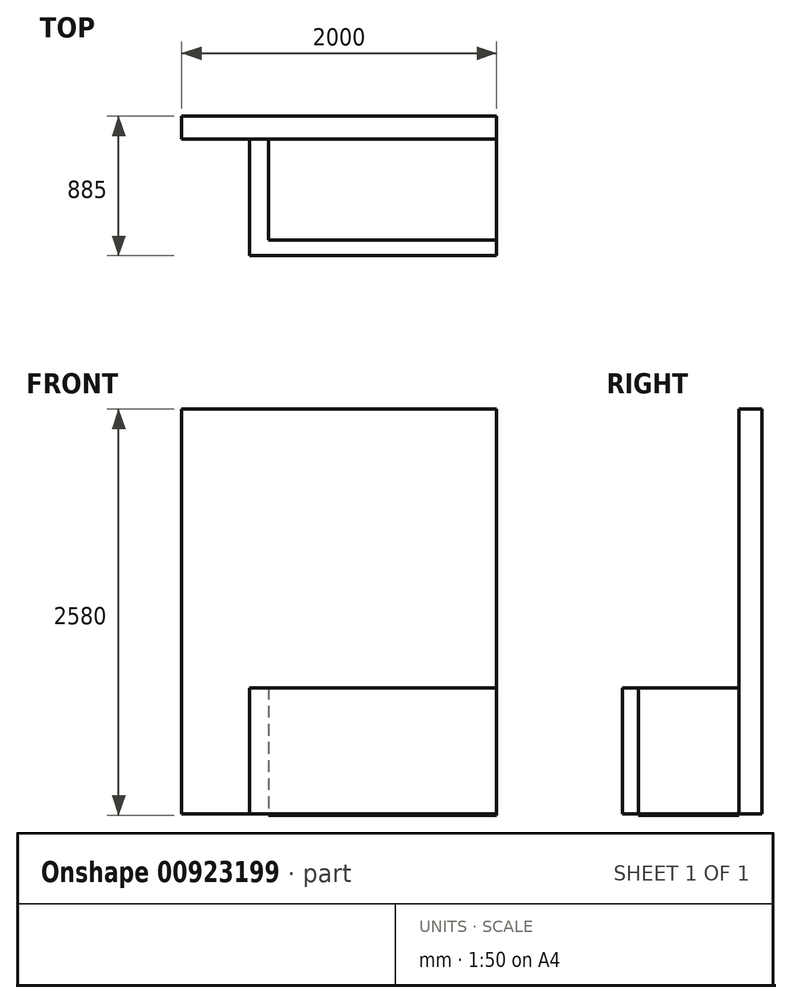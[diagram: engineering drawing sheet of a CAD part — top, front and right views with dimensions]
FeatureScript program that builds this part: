
annotation { "Feature Type Name" : "Feature", "Feature Type Description" : "" }
export const myFeature = defineFeature(function(context is Context, id is Id, definition is map)
    precondition{}
    {
        {
            var Q0;
            Q0=qCreatedBy(makeId("Front.planeOp"),FACE);
            var sketch = newSketch(context, id + "F0", { "sketchPlane" : qUnion([Q0])});
            skLineSegment(sketch, "E0.bottom", {"start": v(-1011, 2269.46) * mm, "end": v(989, 2269.46) * mm});
            skLineSegment(sketch, "E0.top", {"start": v(-1011, -300.54) * mm, "end": v(989, -300.54) * mm});
            skLineSegment(sketch, "E0.left", {"start": v(-1011, 2269.46) * mm, "end": v(-1011, -300.54) * mm});
            skLineSegment(sketch, "E0.right", {"start": v(989, 2269.46) * mm, "end": v(989, -300.54) * mm});
            skSolve(sketch);
        }
        {
            var Q0;
            Q0 = qSketchRegion(id + "F0", true);
            extrude(context, id + "F1", {"entities" : qUnion([Q0]), "oppositeDirection" : true, "depth" : 145 * mm, "offsetDistance" : 25 * mm});
        }
        {
            var Q0;
            Q0=makeQuery(id+"F1.opExtrude","CAP_FACE",FACE,{"disambiguationData":[OSD([sQuery(id+"F0.wireOp",EDGE,"E0.bottom"),sQuery(id+"F0.wireOp",EDGE,"E0.top"),sQuery(id+"F0.wireOp",EDGE,"E0.left"),sQuery(id+"F0.wireOp",EDGE,"E0.right")])],"isStart":true});
            var sketch = newSketch(context, id + "F2", { "sketchPlane" : qUnion([Q0])});
            skLineSegment(sketch, "E1.bottom", {"start": v(-581, 499.46) * mm, "end": v(-461, 499.46) * mm});
            skLineSegment(sketch, "E1.top", {"start": v(-581, -300.54) * mm, "end": v(-461, -300.54) * mm});
            skLineSegment(sketch, "E1.left", {"start": v(-581, 499.46) * mm, "end": v(-581, -300.54) * mm});
            skLineSegment(sketch, "E1.right", {"start": v(-461, 499.46) * mm, "end": v(-461, -300.54) * mm});
            skSolve(sketch);
        }
        {
            var Q0;
            Q0 = qSketchRegion(id + "F2", true);
            extrude(context, id + "F3", {"entities" : qUnion([Q0]), "operationType" : NewBodyOperationType.ADD, "depth" : 740 * mm, "offsetDistance" : 25 * mm});
        }
        {
            var Q0;
            Q0=makeQuery(id+"F3.opExtrude","SWEPT_FACE",FACE,{"disambiguationData":[OSD([sQuery(id+"F2.wireOp",EDGE,"E1.right")])]});
            var sketch = newSketch(context, id + "F4", { "sketchPlane" : qUnion([Q0])});
            skLineSegment(sketch, "E2.bottom", {"start": v(-740, 499.46) * mm, "end": v(-640, 499.46) * mm});
            skLineSegment(sketch, "E2.top", {"start": v(-740, -300.54) * mm, "end": v(-640, -300.54) * mm});
            skLineSegment(sketch, "E2.left", {"start": v(-740, 499.46) * mm, "end": v(-740, -300.54) * mm});
            skLineSegment(sketch, "E2.right", {"start": v(-640, 499.46) * mm, "end": v(-640, -300.54) * mm});
            skSolve(sketch);
        }
        {
            var Q0;
            Q0 = qSketchRegion(id + "F4", true);
            extrude(context, id + "F5", {"entities" : qUnion([Q0]), "operationType" : NewBodyOperationType.ADD, "depth" : 1450 * mm, "offsetDistance" : 25 * mm});
        }
        {
            var Q0;
            Q0=makeQuery(id+"F5.boolean.opBoolean","MERGE",FACE,{"derivedFrom":[makeQuery(id+"F3.boolean.opBoolean","MERGE",FACE,{"derivedFrom":[makeQuery(id+"F1.opExtrude","SWEPT_FACE",FACE,{"disambiguationData":[OSD([sQuery(id+"F0.wireOp",EDGE,"E0.top")])]}),makeQuery(id+"F3.opExtrude","SWEPT_FACE",FACE,{"disambiguationData":[OSD([sQuery(id+"F2.wireOp",EDGE,"E1.top")])]})]}),makeQuery(id+"F5.opExtrude","SWEPT_FACE",FACE,{"disambiguationData":[OSD([sQuery(id+"F4.wireOp",EDGE,"E2.top")])]})]});
            var sketch = newSketch(context, id + "F6", { "sketchPlane" : qUnion([Q0])});
            skLineSegment(sketch, "E3.bottom", {"start": v(-461, 640) * mm, "end": v(989, 640) * mm});
            skLineSegment(sketch, "E3.top", {"start": v(-461, 0) * mm, "end": v(989, 0) * mm});
            skLineSegment(sketch, "E3.left", {"start": v(-461, 640) * mm, "end": v(-461, 0) * mm});
            skLineSegment(sketch, "E3.right", {"start": v(989, 640) * mm, "end": v(989, 0) * mm});
            skSolve(sketch);
        }
        {
            var Q0;
            Q0 = qSketchRegion(id + "F6", true);
            extrude(context, id + "F7", {"entities" : qUnion([Q0]), "depth" : 10 * mm, "offsetDistance" : 25 * mm});
        }
    });
